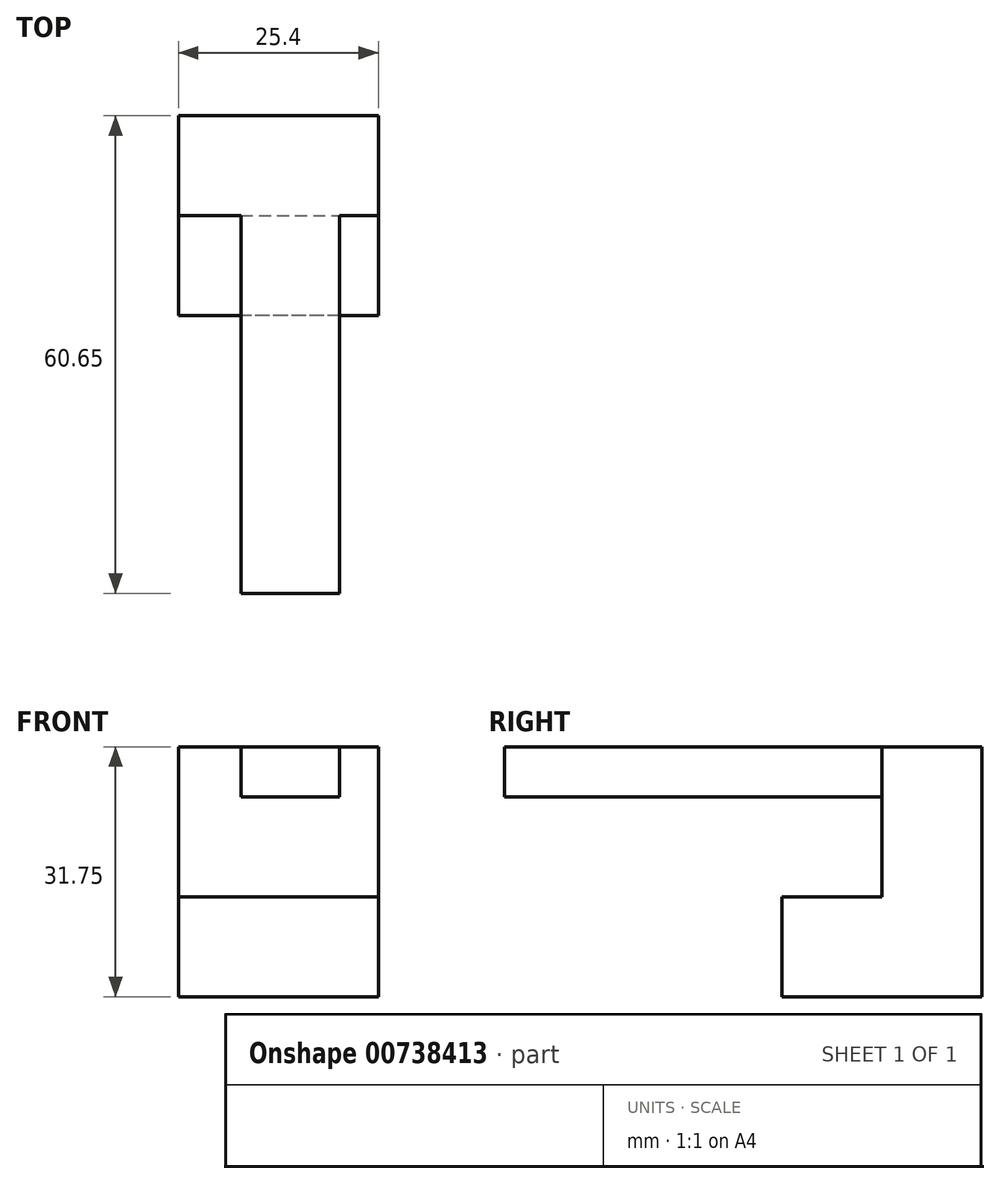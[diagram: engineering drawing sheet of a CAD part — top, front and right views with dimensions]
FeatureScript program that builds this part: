
annotation { "Feature Type Name" : "Feature", "Feature Type Description" : "" }
export const myFeature = defineFeature(function(context is Context, id is Id, definition is map)
    precondition{}
    {
        {
            var Q0;
            Q0=qCreatedBy(makeId("Right.planeOp"),FACE);
            var sketch = newSketch(context, id + "F0", { "sketchPlane" : qUnion([Q0])});
            skLineSegment(sketch, "E0", {"start": v(0, 31.75) * mm, "end": v(0, 0) * mm});
            skLineSegment(sketch, "E1", {"start": v(0, 0) * mm, "end": v(-25.4, 0) * mm});
            skLineSegment(sketch, "E2", {"start": v(-25.4, 0) * mm, "end": v(-25.4, 12.7) * mm});
            skLineSegment(sketch, "E3", {"start": v(-25.4, 12.7) * mm, "end": v(-12.7, 12.7) * mm});
            skLineSegment(sketch, "E4", {"start": v(-12.7, 12.7) * mm, "end": v(-12.7, 31.75) * mm});
            skLineSegment(sketch, "E5", {"start": v(-12.7, 31.75) * mm, "end": v(0, 31.75) * mm});
            skSolve(sketch);
        }
        {
            var Q0;
            Q0 = qSketchRegion(id + "F0", true);
            extrude(context, id + "F1", {"entities" : qUnion([Q0]), "depth" : 25.4 * mm, "offsetDistance" : 25.4 * mm});
        }
        {
            var Q0;
            Q0=makeQuery(id+"F1.opExtrude","SWEPT_FACE",FACE,{"disambiguationData":[OSD([sQuery(id+"F0.wireOp",EDGE,"E4")])]});
            var sketch = newSketch(context, id + "F2", { "sketchPlane" : qUnion([Q0])});
            skLineSegment(sketch, "E6", {"start": v(7.94, 31.75) * mm, "end": v(7.94, 25.4) * mm});
            skLineSegment(sketch, "E7", {"start": v(7.74, 25.4) * mm, "end": v(20.44, 25.4) * mm});
            skLineSegment(sketch, "E8", {"start": v(20.44, 25.4) * mm, "end": v(20.44, 31.75) * mm});
            skSolve(sketch);
        }
        {
            var Q0;
            {var subQ0=sQuery(id+"F2.wireOp",EDGE,"E6");Q0=makeQuery(id+"F2.imprint","IMPRINT",FACE,{"disambiguationData":[TD([[makeQuery(id+"F2.imprint","IMPRINT",EDGE,{"derivedFrom":subQ0}),1.0]])]});}
            var sketch = newSketch(context, id + "F3", { "sketchPlane" : qUnion([Q0])});
            skSolve(sketch);
        }
        {
            var Q0;
            {var subQ0=sQuery(id+"F2.wireOp",EDGE,"E6");Q0=makeQuery(id+"F3.imprint","IMPRINT",FACE,{"disambiguationData":[TD([[makeQuery(id+"F3.imprint","IMPRINT",EDGE,{"derivedFrom":makeQuery(id+"F2.imprint","IMPRINT",EDGE,{"derivedFrom":subQ0})}),1.0]])]});}
            extrude(context, id + "F4", {"entities" : qUnion([Q0]), "operationType" : NewBodyOperationType.ADD, "endBound" : BoundingType.THROUGH_ALL, "depth" : 25.4 * mm, "offsetDistance" : 25.4 * mm});
        }
    });
